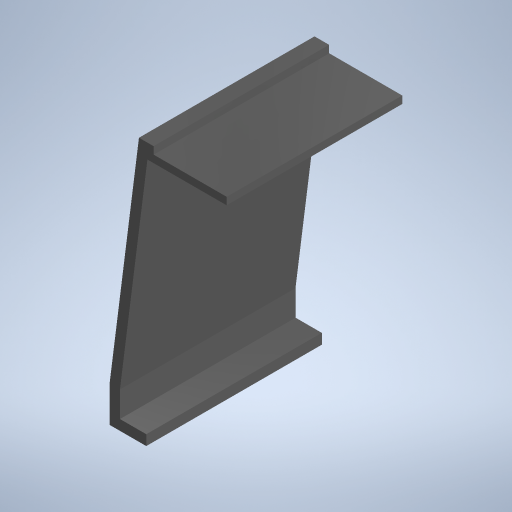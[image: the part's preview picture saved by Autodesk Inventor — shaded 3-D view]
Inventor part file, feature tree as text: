
AUTODESK INVENTOR PART (.ipt)
format: ipt  version: 2023 (Build 270158000, 158)  size: 224,768 bytes
history: native  units: mm (DEFAULTED — no unit token found)
features: other x8, extrude x1, sketch x1
bodies: Solido1 (feature_tree)
feature tree (10):
  other  "Origine"
  extrude  "Estrusione1"  Depth=7.0mm
  other  "Piano YZ"
  other  "Piano XZ"
  other  "Piano XY"
  other  "Asse X"
  other  "Asse Y"
  other  "Asse Z"
  other  "Punto centrale"
  sketch  "Schizzo1"
